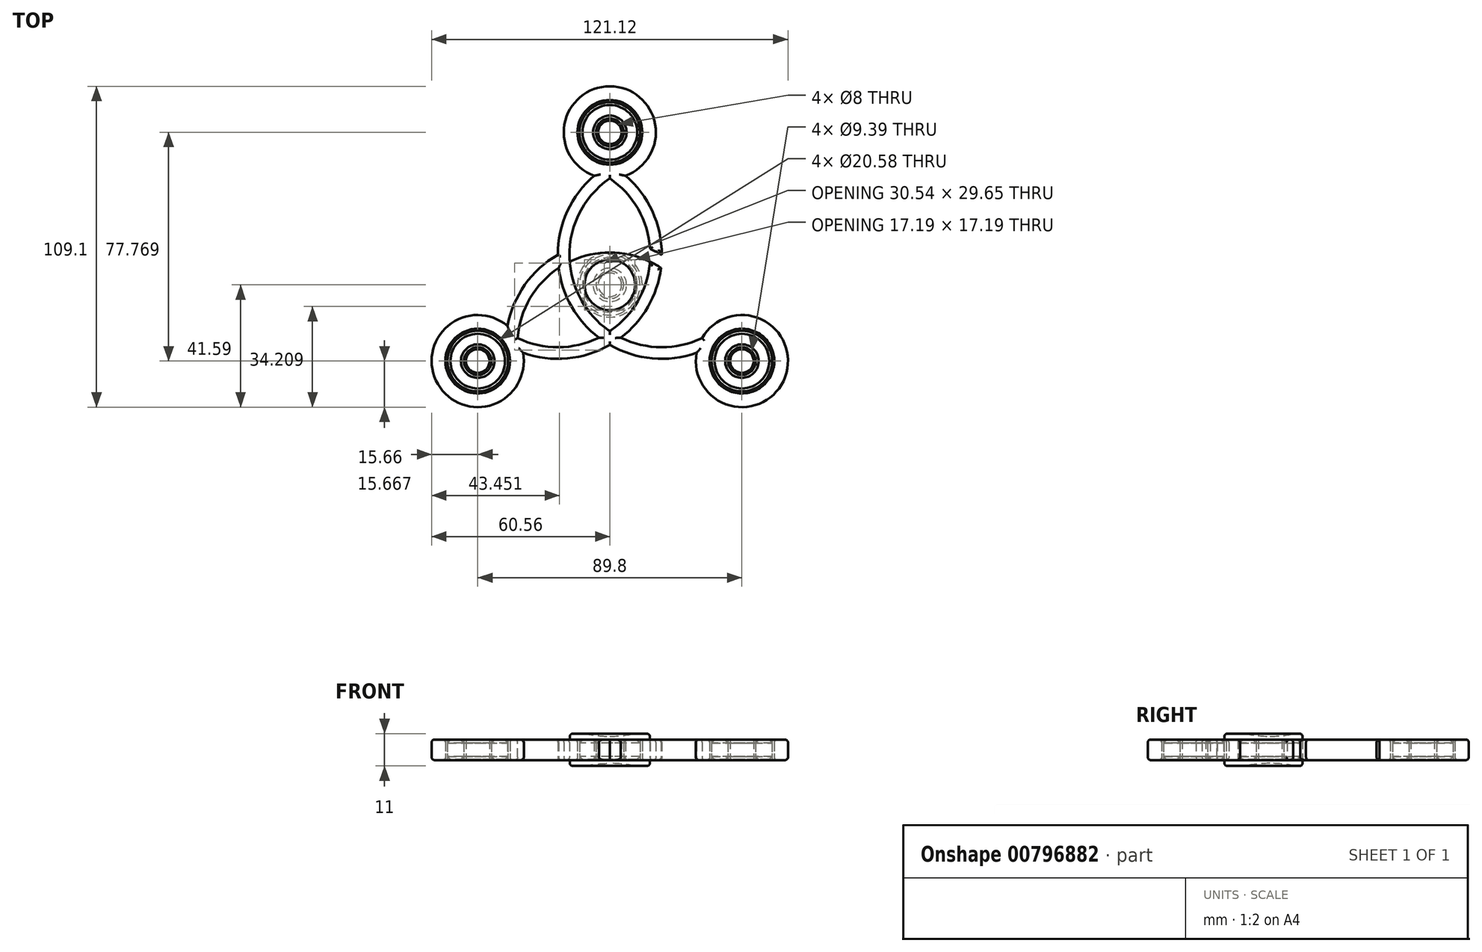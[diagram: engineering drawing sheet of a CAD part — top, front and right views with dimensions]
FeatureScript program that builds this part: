
annotation { "Feature Type Name" : "Feature", "Feature Type Description" : "" }
export const myFeature = defineFeature(function(context is Context, id is Id, definition is map)
    precondition{}
    {
        {
            var Q0;
            Q0=qCreatedBy(makeId("Front.planeOp"),FACE);
            var sketch = newSketch(context, id + "F0", { "sketchPlane" : qUnion([Q0])});
            skLineSegment(sketch, "E0", {"start": v(0, 0) * mm, "end": v(0, 16.34) * mm, "construction": true});
            skSolve(sketch);
        }
        {
            var Q0;
            Q0=qCreatedBy(makeId("Top.planeOp"),FACE);
            var sketch = newSketch(context, id + "F1", { "sketchPlane" : qUnion([Q0])});
            skCircle(sketch, "E1.cCircle", {"center": v(0, 0) * mm, "radius": 40.85 * mm, "construction": true});
            skLineSegment(sketch, "E1.0", {"start": v(0, 40.85) * mm, "end": v(35.37, -20.42) * mm, "construction": true});
            skLineSegment(sketch, "E1.1", {"start": v(35.37, -20.42) * mm, "end": v(-35.37, -20.42) * mm, "construction": true});
            skLineSegment(sketch, "E1.2", {"start": v(-35.37, -20.42) * mm, "end": v(0, 40.85) * mm, "construction": true});
            skCircle(sketch, "E2", {"center": v(0, 40.85) * mm, "radius": 11 * mm, "construction": true});
            skCircle(sketch, "E3", {"center": v(35.37, -20.42) * mm, "radius": 11 * mm, "construction": true});
            skCircle(sketch, "E4", {"center": v(-35.37, -20.42) * mm, "radius": 11 * mm, "construction": true});
            skCircle(sketch, "E5", {"center": v(0, 0) * mm, "radius": 11 * mm, "construction": true});
            skArc(sketch, "E6", {"start": v(10.27, 44.8) * mm, "mid": v(-15.33, -2.5) * mm, "end": v(35.37, -20.42) * mm});
            skArc(sketch, "E7", {"start": v(-35.37, -20.42) * mm, "mid": v(15.33, -2.5) * mm, "end": v(-10.27, 44.8) * mm});
            skArc(sketch, "E8", {"start": v(35.37, -20.42) * mm, "mid": v(0, 14.95) * mm, "end": v(-35.37, -20.42) * mm});
            skLineSegment(sketch, "E9", {"start": v(-35.37, -20.42) * mm, "end": v(-12.95, -7.48) * mm, "construction": true});
            skLineSegment(sketch, "E10.trimOffspring", {"start": v(-9.53, -5.5) * mm, "end": v(0, 0) * mm, "construction": true});
            skLineSegment(sketch, "E11", {"start": v(-12.95, -7.48) * mm, "end": v(-9.53, -5.5) * mm, "construction": true});
            skArc(sketch, "E12.0", {"start": v(11.1, 40.94) * mm, "mid": v(-11.27, -2) * mm, "end": v(35.1, -15.95) * mm});
            skArc(sketch, "E13.0", {"start": v(30.75, -26.88) * mm, "mid": v(-1.6, 10.96) * mm, "end": v(-29.93, -29.98) * mm});
            skArc(sketch, "E14.0", {"start": v(-41, -10.86) * mm, "mid": v(-40.97, -10.9) * mm, "end": v(-40.93, -10.93) * mm});
            skArc(sketch, "E15.trimOffspring", {"start": v(40.93, -10.93) * mm, "mid": v(40.97, -10.9) * mm, "end": v(41, -10.86) * mm});
            skArc(sketch, "E16.trimOffspring", {"start": v(-35.1, -15.95) * mm, "mid": v(11.27, -2) * mm, "end": v(-11.1, 40.94) * mm});
            skLineSegment(sketch, "E17", {"start": v(0, 40.85) * mm, "end": v(0, 36.18) * mm, "construction": true});
            skSolve(sketch);
        }
        {
            var Q0;
            {var subQ0=sQuery(id+"F1.wireOp",EDGE,"E13.0");var subQ1=sQuery(id+"F1.wireOp",EDGE,"E6");var subQ2=makeQuery(id+"F1.imprint","INTERSECT",VERTEX,{"disambiguationData":[OD(0.0)],"derivedFrom":[subQ1,subQ0]});Q0=makeQuery(id+"F1.imprint","IMPRINT",FACE,{"disambiguationData":[TD([[makeQuery(id+"F1.imprint","IMPRINT",EDGE,{"disambiguationData":[TD([[subQ2,1.0]])],"derivedFrom":subQ1}),1.0]])]});}
            var Q1;
            {var subQ0=sQuery(id+"F1.wireOp",EDGE,"E7");var subQ1=sQuery(id+"F1.wireOp",EDGE,"E6");var subQ2=makeQuery(id+"F1.imprint","INTERSECT",VERTEX,{"disambiguationData":[OD(1.0)],"derivedFrom":[subQ1,subQ0]});Q1=makeQuery(id+"F1.imprint","IMPRINT",FACE,{"disambiguationData":[TD([[makeQuery(id+"F1.imprint","IMPRINT",EDGE,{"disambiguationData":[TD([[subQ2,1.0]])],"derivedFrom":subQ1}),1.0]])]});}
            var Q2;
            {var subQ0=sQuery(id+"F1.wireOp",EDGE,"E7");var subQ1=sQuery(id+"F1.wireOp",EDGE,"E6");var subQ2=makeQuery(id+"F1.imprint","INTERSECT",VERTEX,{"disambiguationData":[OD(1.0)],"derivedFrom":[subQ1,subQ0]});Q2=makeQuery(id+"F1.imprint","IMPRINT",FACE,{"disambiguationData":[TD([[makeQuery(id+"F1.imprint","IMPRINT",EDGE,{"disambiguationData":[TD([[subQ2,1.0]])],"derivedFrom":subQ1}),-1.0]])]});}
            var Q3;
            {var subQ0=sQuery(id+"F1.wireOp",EDGE,"E8");var subQ1=sQuery(id+"F1.wireOp",EDGE,"E7");var subQ2=makeQuery(id+"F1.imprint","INTERSECT",VERTEX,{"disambiguationData":[OD(0.0)],"derivedFrom":[subQ1,subQ0]});Q3=makeQuery(id+"F1.imprint","IMPRINT",FACE,{"disambiguationData":[TD([[makeQuery(id+"F1.imprint","IMPRINT",EDGE,{"disambiguationData":[TD([[subQ2,-1.0]])],"derivedFrom":subQ1}),1.0]])]});}
            var Q4;
            {var subQ0=sQuery(id+"F1.wireOp",EDGE,"E8");var subQ1=sQuery(id+"F1.wireOp",EDGE,"E6");var subQ2=makeQuery(id+"F1.imprint","INTERSECT",VERTEX,{"disambiguationData":[OD(1.0)],"derivedFrom":[subQ1,subQ0]});Q4=makeQuery(id+"F1.imprint","IMPRINT",FACE,{"disambiguationData":[TD([[makeQuery(id+"F1.imprint","IMPRINT",EDGE,{"disambiguationData":[TD([[subQ2,-1.0]])],"derivedFrom":subQ1}),-1.0]])]});}
            var Q5;
            {var subQ0=sQuery(id+"F1.wireOp",EDGE,"E13.0");var subQ1=sQuery(id+"F1.wireOp",EDGE,"E6");var subQ2=makeQuery(id+"F1.imprint","INTERSECT",VERTEX,{"disambiguationData":[OD(1.0)],"derivedFrom":[subQ1,subQ0]});Q5=makeQuery(id+"F1.imprint","IMPRINT",FACE,{"disambiguationData":[TD([[makeQuery(id+"F1.imprint","IMPRINT",EDGE,{"disambiguationData":[TD([[subQ2,-1.0]])],"derivedFrom":subQ1}),1.0]])]});}
            var Q6;
            {var subQ0=sQuery(id+"F1.wireOp",EDGE,"E8");var subQ1=sQuery(id+"F1.wireOp",EDGE,"E6");var subQ2=makeQuery(id+"F1.imprint","INTERSECT",VERTEX,{"disambiguationData":[OD(1.0)],"derivedFrom":[subQ1,subQ0]});Q6=makeQuery(id+"F1.imprint","IMPRINT",FACE,{"disambiguationData":[TD([[makeQuery(id+"F1.imprint","IMPRINT",EDGE,{"disambiguationData":[TD([[subQ2,-1.0]])],"derivedFrom":subQ1}),1.0]])]});}
            var Q7;
            {var subQ0=sQuery(id+"F1.wireOp",EDGE,"E12.0");var subQ1=sQuery(id+"F1.wireOp",EDGE,"E7");var subQ2=makeQuery(id+"F1.imprint","INTERSECT",VERTEX,{"disambiguationData":[OD(1.0)],"derivedFrom":[subQ1,subQ0]});Q7=makeQuery(id+"F1.imprint","IMPRINT",FACE,{"disambiguationData":[TD([[makeQuery(id+"F1.imprint","IMPRINT",EDGE,{"disambiguationData":[TD([[subQ2,-1.0]])],"derivedFrom":subQ1}),1.0]])]});}
            var Q8;
            {var subQ0=sQuery(id+"F1.wireOp",EDGE,"E8");var subQ1=sQuery(id+"F1.wireOp",EDGE,"E6");var subQ2=makeQuery(id+"F1.imprint","INTERSECT",VERTEX,{"disambiguationData":[OD(0.0)],"derivedFrom":[subQ1,subQ0]});Q8=makeQuery(id+"F1.imprint","IMPRINT",FACE,{"disambiguationData":[TD([[makeQuery(id+"F1.imprint","IMPRINT",EDGE,{"disambiguationData":[TD([[subQ2,1.0]])],"derivedFrom":subQ1}),1.0]])]});}
            var Q9;
            {var subQ0=sQuery(id+"F1.wireOp",EDGE,"E8");var subQ1=sQuery(id+"F1.wireOp",EDGE,"E7");var subQ2=makeQuery(id+"F1.imprint","INTERSECT",VERTEX,{"disambiguationData":[OD(1.0)],"derivedFrom":[subQ1,subQ0]});Q9=makeQuery(id+"F1.imprint","IMPRINT",FACE,{"disambiguationData":[TD([[makeQuery(id+"F1.imprint","IMPRINT",EDGE,{"disambiguationData":[TD([[subQ2,1.0]])],"derivedFrom":subQ1}),-1.0]])]});}
            var Q10;
            {var subQ0=sQuery(id+"F1.wireOp",EDGE,"E8");var subQ1=sQuery(id+"F1.wireOp",EDGE,"E7");var subQ2=makeQuery(id+"F1.imprint","INTERSECT",VERTEX,{"disambiguationData":[OD(1.0)],"derivedFrom":[subQ1,subQ0]});Q10=makeQuery(id+"F1.imprint","IMPRINT",FACE,{"disambiguationData":[TD([[makeQuery(id+"F1.imprint","IMPRINT",EDGE,{"disambiguationData":[TD([[subQ2,1.0]])],"derivedFrom":subQ1}),1.0]])]});}
            var Q11;
            {var subQ0=sQuery(id+"F1.wireOp",EDGE,"E16.trimOffspring");var subQ1=sQuery(id+"F1.wireOp",EDGE,"E8");var subQ2=makeQuery(id+"F1.imprint","INTERSECT",VERTEX,{"disambiguationData":[OD(1.0)],"derivedFrom":[subQ1,subQ0]});Q11=makeQuery(id+"F1.imprint","IMPRINT",FACE,{"disambiguationData":[TD([[makeQuery(id+"F1.imprint","IMPRINT",EDGE,{"disambiguationData":[TD([[subQ2,-1.0]])],"derivedFrom":subQ1}),1.0]])]});}
            var Q12;
            {var subQ0=sQuery(id+"F1.wireOp",EDGE,"E16.trimOffspring");var subQ1=sQuery(id+"F1.wireOp",EDGE,"E6");var subQ2=makeQuery(id+"F1.imprint","INTERSECT",VERTEX,{"disambiguationData":[OD(0.0)],"derivedFrom":[subQ1,subQ0]});Q12=makeQuery(id+"F1.imprint","IMPRINT",FACE,{"disambiguationData":[TD([[makeQuery(id+"F1.imprint","IMPRINT",EDGE,{"disambiguationData":[TD([[subQ2,-1.0]])],"derivedFrom":subQ1}),1.0]])]});}
            var Q13;
            {var subQ0=sQuery(id+"F1.wireOp",EDGE,"E7");var subQ1=sQuery(id+"F1.wireOp",EDGE,"E6");var subQ2=makeQuery(id+"F1.imprint","INTERSECT",VERTEX,{"disambiguationData":[OD(0.0)],"derivedFrom":[subQ1,subQ0]});Q13=makeQuery(id+"F1.imprint","IMPRINT",FACE,{"disambiguationData":[TD([[makeQuery(id+"F1.imprint","IMPRINT",EDGE,{"disambiguationData":[TD([[subQ2,-1.0]])],"derivedFrom":subQ1}),1.0]])]});}
            var Q14;
            {var subQ0=sQuery(id+"F1.wireOp",EDGE,"E12.0");var subQ1=sQuery(id+"F1.wireOp",EDGE,"E7");var subQ2=makeQuery(id+"F1.imprint","INTERSECT",VERTEX,{"disambiguationData":[OD(0.0)],"derivedFrom":[subQ1,subQ0]});Q14=makeQuery(id+"F1.imprint","IMPRINT",FACE,{"disambiguationData":[TD([[makeQuery(id+"F1.imprint","IMPRINT",EDGE,{"disambiguationData":[TD([[subQ2,1.0]])],"derivedFrom":subQ1}),1.0]])]});}
            extrude(context, id + "F2", {"entities" : qUnion([Q0, Q1, Q2, Q3, Q4, Q5, Q6, Q7, Q8, Q9, Q10, Q11, Q12, Q13, Q14]), "endBound" : BoundingType.SYMMETRIC, "depth" : 7 * mm, "offsetDistance" : 25 * mm});
        }
        {
            var Q0;
            Q0=qCreatedBy(makeId("Top.planeOp"),FACE);
            var sketch = newSketch(context, id + "F3", { "sketchPlane" : qUnion([Q0])});
            skLineSegment(sketch, "E18", {"start": v(0, 0) * mm, "end": v(0, 40.85) * mm, "construction": true});
            skLineSegment(sketch, "E19", {"start": v(0, 40.85) * mm, "end": v(0, 51.85) * mm, "construction": true});
            skCircle(sketch, "E20", {"center": v(0, 51.85) * mm, "radius": 11 * mm});
            skCircle(sketch, "E21.0", {"center": v(0, 51.85) * mm, "radius": 15.66 * mm});
            skCircle(sketch, "E22.1.0", {"center": v(-44.9, -25.92) * mm, "radius": 11 * mm});
            skCircle(sketch, "E22.1.1", {"center": v(-44.9, -25.92) * mm, "radius": 15.66 * mm});
            skCircle(sketch, "E22.2.0", {"center": v(44.9, -25.92) * mm, "radius": 11 * mm});
            skCircle(sketch, "E22.2.1", {"center": v(44.9, -25.92) * mm, "radius": 15.66 * mm});
            skPoint(sketch, "E22.center", {"position": v(0, 0) * mm});
            skSolve(sketch);
        }
        {
            var Q0;
            Q0=qSketchRegion(id+"F3",true);
            extrude(context, id + "F4", {"entities" : qUnion([Q0]), "operationType" : NewBodyOperationType.ADD, "endBound" : BoundingType.SYMMETRIC, "depth" : 7 * mm, "offsetDistance" : 25 * mm});
        }
        {
            var Q0;
            Q0=makeQuery(id+"F4.boolean.opBoolean","MERGE",FACE,{"derivedFrom":[makeQuery(id+"F2.opExtrude","CAP_FACE",FACE,{"disambiguationData":[OSD([sQuery(id+"F1.wireOp",EDGE,"E6"),sQuery(id+"F1.wireOp",EDGE,"E7"),sQuery(id+"F1.wireOp",EDGE,"E8"),sQuery(id+"F1.wireOp",EDGE,"E12.0"),sQuery(id+"F1.wireOp",EDGE,"E13.0"),sQuery(id+"F1.wireOp",EDGE,"E16.trimOffspring")])],"isStart":true}),makeQuery(id+"F4.opExtrude","CAP_FACE",FACE,{"disambiguationData":[OSD([sQuery(id+"F3.wireOp",EDGE,"E20"),sQuery(id+"F3.wireOp",EDGE,"E21.0")])],"isStart":true}),makeQuery(id+"F4.opExtrude","CAP_FACE",FACE,{"disambiguationData":[OSD([sQuery(id+"F3.wireOp",EDGE,"E22.1.0"),sQuery(id+"F3.wireOp",EDGE,"E22.1.1")])],"isStart":true}),makeQuery(id+"F4.opExtrude","CAP_FACE",FACE,{"disambiguationData":[OSD([sQuery(id+"F3.wireOp",EDGE,"E22.2.0"),sQuery(id+"F3.wireOp",EDGE,"E22.2.1")])],"isStart":true})]});
            var Q1;
            Q1=makeQuery(id+"F4.boolean.opBoolean","MERGE",FACE,{"derivedFrom":[makeQuery(id+"F2.opExtrude","CAP_FACE",FACE,{"disambiguationData":[OSD([sQuery(id+"F1.wireOp",EDGE,"E6"),sQuery(id+"F1.wireOp",EDGE,"E7"),sQuery(id+"F1.wireOp",EDGE,"E8"),sQuery(id+"F1.wireOp",EDGE,"E12.0"),sQuery(id+"F1.wireOp",EDGE,"E13.0"),sQuery(id+"F1.wireOp",EDGE,"E16.trimOffspring")])],"isStart":false}),makeQuery(id+"F4.opExtrude","CAP_FACE",FACE,{"disambiguationData":[OSD([sQuery(id+"F3.wireOp",EDGE,"E20"),sQuery(id+"F3.wireOp",EDGE,"E21.0")])],"isStart":false}),makeQuery(id+"F4.opExtrude","CAP_FACE",FACE,{"disambiguationData":[OSD([sQuery(id+"F3.wireOp",EDGE,"E22.1.0"),sQuery(id+"F3.wireOp",EDGE,"E22.1.1")])],"isStart":false}),makeQuery(id+"F4.opExtrude","CAP_FACE",FACE,{"disambiguationData":[OSD([sQuery(id+"F3.wireOp",EDGE,"E22.2.0"),sQuery(id+"F3.wireOp",EDGE,"E22.2.1")])],"isStart":false})]});
            fillet(context, id + "F5", {"entities" : qUnion([Q0, Q1]), "radius" : 1 * mm, "tangentPropagation" : true, "allowEdgeOverflow" : false});
        }
        {
            var Q0;
            Q0=qCreatedBy(makeId("Top.planeOp"),FACE);
            var sketch = newSketch(context, id + "F6", { "sketchPlane" : qUnion([Q0])});
            skCircle(sketch, "E23", {"center": v(0, 0) * mm, "radius": 11 * mm});
            skCircle(sketch, "E24", {"center": v(0, 0) * mm, "radius": 4 * mm});
            skCircle(sketch, "E25", {"center": v(0, 0) * mm, "radius": 4.7 * mm});
            skCircle(sketch, "E26", {"center": v(0, 0) * mm, "radius": 10.3 * mm});
            skSolve(sketch);
        }
        {
            var Q0;
            Q0=makeQuery(id+"F6.imprint","IMPRINT",FACE,{"disambiguationData":[TD([[makeQuery(id+"F6.imprint","IMPRINT",EDGE,{"derivedFrom":sQuery(id+"F6.wireOp",EDGE,"E24")}),-1.0]])]});
            var Q1;
            Q1=makeQuery(id+"F6.imprint","IMPRINT",FACE,{"disambiguationData":[TD([[makeQuery(id+"F6.imprint","IMPRINT",EDGE,{"derivedFrom":sQuery(id+"F6.wireOp",EDGE,"E23")}),1.0]])]});
            extrude(context, id + "F7", {"entities" : qUnion([Q0, Q1]), "operationType" : NewBodyOperationType.ADD, "endBound" : BoundingType.SYMMETRIC, "depth" : 7 * mm, "offsetDistance" : 25 * mm});
        }
        {
            var Q0;
            Q0=makeQuery(id+"F6.imprint","IMPRINT",FACE,{"disambiguationData":[TD([[makeQuery(id+"F6.imprint","IMPRINT",EDGE,{"derivedFrom":sQuery(id+"F6.wireOp",EDGE,"E25")}),-1.0]])]});
            extrude(context, id + "F8", {"entities" : qUnion([Q0]), "endBound" : BoundingType.SYMMETRIC, "depth" : 6.5 * mm, "offsetDistance" : 25 * mm});
        }
        {
            var Q0;
            Q0=makeQuery(id+"F8.opExtrude","CAP_EDGE",EDGE,{"disambiguationData":[OSD([sQuery(id+"F6.wireOp",EDGE,"E26")])],"isStart":false});
            var Q1;
            Q1=makeQuery(id+"F8.opExtrude","CAP_EDGE",EDGE,{"disambiguationData":[OSD([sQuery(id+"F6.wireOp",EDGE,"E25")])],"isStart":false});
            chamfer(context, id + "F9", {"entities" : qUnion([Q0, Q1]), "chamferType" : ChamferType.OFFSET_ANGLE, "width" : 1 * mm, "oppositeDirection" : false, "angle" : 45 * degree, "tangentPropagation" : true});
        }
        {
            var Q0;
            Q0=makeQuery(id+"F8.opExtrude","CAP_EDGE",EDGE,{"disambiguationData":[OSD([sQuery(id+"F6.wireOp",EDGE,"E25")])],"isStart":true});
            var Q1;
            Q1=makeQuery(id+"F8.opExtrude","CAP_EDGE",EDGE,{"disambiguationData":[OSD([sQuery(id+"F6.wireOp",EDGE,"E26")])],"isStart":true});
            chamfer(context, id + "F10", {"entities" : qUnion([Q0, Q1]), "width" : 1 * mm, "tangentPropagation" : true});
        }
        {
            var Q0;
            Q0=makeQuery(id+"F7.opExtrude","CAP_EDGE",EDGE,{"disambiguationData":[OSD([sQuery(id+"F6.wireOp",EDGE,"E23")])],"isStart":false});
            var Q1;
            Q1=makeQuery(id+"F7.opExtrude","CAP_EDGE",EDGE,{"disambiguationData":[OSD([sQuery(id+"F6.wireOp",EDGE,"E26")])],"isStart":false});
            fillet(context, id + "F11", {"entities" : qUnion([Q0, Q1]), "radius" : .2 * mm, "tangentPropagation" : true, "allowEdgeOverflow" : false});
        }
        {
            var Q0;
            Q0=makeQuery(id+"F7.opExtrude","CAP_EDGE",EDGE,{"disambiguationData":[OSD([sQuery(id+"F6.wireOp",EDGE,"E24")])],"isStart":false});
            var Q1;
            Q1=makeQuery(id+"F7.opExtrude","CAP_EDGE",EDGE,{"disambiguationData":[OSD([sQuery(id+"F6.wireOp",EDGE,"E25")])],"isStart":false});
            var Q2;
            Q2=makeQuery(id+"F7.opExtrude","CAP_EDGE",EDGE,{"disambiguationData":[OSD([sQuery(id+"F6.wireOp",EDGE,"E23")])],"isStart":true});
            var Q3;
            Q3=makeQuery(id+"F7.opExtrude","CAP_EDGE",EDGE,{"disambiguationData":[OSD([sQuery(id+"F6.wireOp",EDGE,"E26")])],"isStart":true});
            var Q4;
            Q4=makeQuery(id+"F7.opExtrude","CAP_EDGE",EDGE,{"disambiguationData":[OSD([sQuery(id+"F6.wireOp",EDGE,"E25")])],"isStart":true});
            var Q5;
            Q5=makeQuery(id+"F7.opExtrude","CAP_EDGE",EDGE,{"disambiguationData":[OSD([sQuery(id+"F6.wireOp",EDGE,"E24")])],"isStart":true});
            fillet(context, id + "F12", {"entities" : qUnion([Q0, Q1, Q2, Q3, Q4, Q5]), "radius" : .2 * mm, "tangentPropagation" : true, "allowEdgeOverflow" : false});
        }
        {
            var Q0;
            Q0=qCreatedBy(makeId("Top.planeOp"),FACE);
            var sketch = newSketch(context, id + "F13", { "sketchPlane" : qUnion([Q0])});
            skLineSegment(sketch, "E27", {"start": v(0, 0) * mm, "end": v(0, 32) * mm, "construction": true});
            skSolve(sketch);
        }
        {
            var Q0;
            Q0=makeQuery(id+"F7.opExtrude","SWEPT_BODY",BODY,{"disambiguationData":[OSD([sQuery(id+"F6.wireOp",EDGE,"E23"),sQuery(id+"F6.wireOp",EDGE,"E26")])]});
            var Q1;
            Q1=makeQuery(id+"F7.opExtrude","SWEPT_BODY",BODY,{"disambiguationData":[OSD([sQuery(id+"F6.wireOp",EDGE,"E24"),sQuery(id+"F6.wireOp",EDGE,"E25")])]});
            var Q2;
            Q2=makeQuery(id+"F8.opExtrude","SWEPT_BODY",BODY,{"disambiguationData":[OSD([sQuery(id+"F6.wireOp",EDGE,"E25"),sQuery(id+"F6.wireOp",EDGE,"E26")])]});
            var Q3;
            Q3=sQuery(id+"F13.wireOp",EDGE,"E27");
            var Q4;
            Q4=sQuery(id+"F13.wireOp",EDGE,"E27");
            transform(context, id + "F14", {"entities" : qUnion([Q0, Q1, Q2]), "transformType" : TransformType.TRANSLATION_DISTANCE, "transformDirection" : qUnion([Q4]), "distance" : 51.85 * mm, "makeCopy" : true});
        }
        {
            var Q0;
            Q0=makeQuery(id+"F14.opPattern","COPY",BODY,{"derivedFrom":makeQuery(id+"F8.opExtrude","SWEPT_BODY",BODY,{"disambiguationData":[OSD([sQuery(id+"F6.wireOp",EDGE,"E25"),sQuery(id+"F6.wireOp",EDGE,"E26")])]}),"instanceName":"1"});
            var Q1;
            Q1=makeQuery(id+"F14.opPattern","COPY",BODY,{"derivedFrom":makeQuery(id+"F7.opExtrude","SWEPT_BODY",BODY,{"disambiguationData":[OSD([sQuery(id+"F6.wireOp",EDGE,"E24"),sQuery(id+"F6.wireOp",EDGE,"E25")])]}),"instanceName":"1"});
            var Q2;
            Q2=makeQuery(id+"F14.opPattern","COPY",BODY,{"derivedFrom":makeQuery(id+"F7.opExtrude","SWEPT_BODY",BODY,{"disambiguationData":[OSD([sQuery(id+"F6.wireOp",EDGE,"E23"),sQuery(id+"F6.wireOp",EDGE,"E26")])]}),"instanceName":"1"});
            var Q3;
            Q3=sQuery(id+"F0.wireOp",EDGE,"E0");
            circularPattern(context, id + "F15", {"entities" : qUnion([Q0, Q1, Q2]), "axis" : qUnion([Q3]), "angle" : 360 * degree, "instanceCount" : 3, "equalSpace" : true});
        }
        {
            var Q0;
            Q0=makeQuery(id+"F7.opExtrude","CAP_FACE",FACE,{"disambiguationData":[OSD([sQuery(id+"F6.wireOp",EDGE,"E24"),sQuery(id+"F6.wireOp",EDGE,"E25")])],"isStart":false});
            var sketch = newSketch(context, id + "F16", { "sketchPlane" : qUnion([Q0])});
            skArc(sketch, "E28.0", {"start": v(13.65, 7.88) * mm, "mid": v(0, 11) * mm, "end": v(-13.65, 7.88) * mm});
            skArc(sketch, "E29.trimOffspring", {"start": v(0, -15.76) * mm, "mid": v(9.53, -5.5) * mm, "end": v(13.65, 7.88) * mm});
            skArc(sketch, "E30.trimOffspring", {"start": v(-13.65, 7.88) * mm, "mid": v(-9.53, -5.5) * mm, "end": v(0, -15.76) * mm});
            skSolve(sketch);
        }
        {
            var Q0;
            Q0=qSketchRegion(id+"F16",true);
            extrude(context, id + "F17", {"entities" : qUnion([Q0]), "depth" : 2 * mm, "offsetDistance" : 25 * mm});
        }
        {
            var Q0;
            Q0=qCreatedBy(makeId("Front.planeOp"),FACE);
            var sketch = newSketch(context, id + "F18", { "sketchPlane" : qUnion([Q0])});
            skArc(sketch, "E31", {"start": v(0, 4.6) * mm, "mid": v(41.52, 46.12) * mm, "end": v(0, 87.64) * mm});
            skLineSegment(sketch, "E32", {"start": v(0, 46.12) * mm, "end": v(0, 4.6) * mm});
            skLineSegment(sketch, "E33", {"start": v(0, 46.12) * mm, "end": v(0, 87.64) * mm});
            skSolve(sketch);
        }
        {
            var Q0;
            Q0=makeQuery(id+"F18.imprint","IMPRINT",FACE,{"disambiguationData":[TD([[makeQuery(id+"F18.imprint","IMPRINT",EDGE,{"derivedFrom":sQuery(id+"F18.wireOp",EDGE,"E31")}),1.0]])]});
            var Q1;
            Q1=sQuery(id+"F18.wireOp",EDGE,"E33");
            revolve(context, id + "F19", {"surfaceOperationType" : NewSurfaceOperationType.NEW, "entities" : qUnion([Q0]), "axis" : qUnion([Q1]), "revolveType" : RevolveType.FULL});
        }
        {
            var Q0;
            Q0=makeQuery(id+"F19.opRevolve","SWEPT_BODY",BODY,{"disambiguationData":[OSD([sQuery(id+"F18.wireOp",EDGE,"E31"),sQuery(id+"F18.wireOp",EDGE,"E32"),sQuery(id+"F18.wireOp",EDGE,"E33")])]});
            var Q1;
            Q1=makeQuery(id+"F17.opExtrude","SWEPT_BODY",BODY,{"disambiguationData":[OSD([sQuery(id+"F16.wireOp",EDGE,"E28.0"),sQuery(id+"F16.wireOp",EDGE,"E29.trimOffspring"),sQuery(id+"F16.wireOp",EDGE,"E30.trimOffspring")])]});
            booleanBodies(context, id + "F20", {"operationType" : BooleanOperationType.SUBTRACTION, "tools" : qUnion([Q0]), "targets" : qUnion([Q1])});
        }
        {
            var Q0;
            Q0=makeQuery(id+"F17.opExtrude","CAP_EDGE",EDGE,{"disambiguationData":[OSD([sQuery(id+"F16.wireOp",EDGE,"E29.trimOffspring")])],"isStart":false});
            var Q1;
            {var subQ0=sQuery(id+"F1.wireOp",EDGE,"E16.trimOffspring");var subQ1=sQuery(id+"F1.wireOp",EDGE,"E12.0");var subQ2=sQuery(id+"F1.wireOp",EDGE,"E8");Q1=makeQuery(id+"F5.opFillet","BLEND_EDGE",EDGE,{"blendedFrom":[makeQuery(id+"F2.opExtrude","CAP_EDGE",EDGE,{"disambiguationData":[OSD([subQ2]),TDD([makeQuery(id+"F1.imprint","IMPRINT",EDGE,{"disambiguationData":[TD([[makeQuery(id+"F1.imprint","INTERSECT",VERTEX,{"disambiguationData":[OD(1.0)],"derivedFrom":[subQ2,subQ0]}),-1.0]])],"derivedFrom":subQ2})])],"isStart":false}),makeQuery(id+"F4.boolean.opBoolean","MERGE",FACE,{"derivedFrom":[makeQuery(id+"F2.opExtrude","CAP_FACE",FACE,{"disambiguationData":[OSD([sQuery(id+"F1.wireOp",EDGE,"E6"),sQuery(id+"F1.wireOp",EDGE,"E7"),subQ2,subQ1,sQuery(id+"F1.wireOp",EDGE,"E13.0"),subQ0])],"isStart":false}),makeQuery(id+"F4.opExtrude","CAP_FACE",FACE,{"disambiguationData":[OSD([sQuery(id+"F3.wireOp",EDGE,"E20"),sQuery(id+"F3.wireOp",EDGE,"E21.0")])],"isStart":false}),makeQuery(id+"F4.opExtrude","CAP_FACE",FACE,{"disambiguationData":[OSD([sQuery(id+"F3.wireOp",EDGE,"E22.1.0"),sQuery(id+"F3.wireOp",EDGE,"E22.1.1")])],"isStart":false}),makeQuery(id+"F4.opExtrude","CAP_FACE",FACE,{"disambiguationData":[OSD([sQuery(id+"F3.wireOp",EDGE,"E22.2.0"),sQuery(id+"F3.wireOp",EDGE,"E22.2.1")])],"isStart":false})]})],"blendedInto":[makeQuery(id+"F4.boolean.opBoolean","MERGE",FACE,{"derivedFrom":[makeQuery(id+"F2.opExtrude","CAP_FACE",FACE,{"disambiguationData":[OSD([sQuery(id+"F1.wireOp",EDGE,"E6"),sQuery(id+"F1.wireOp",EDGE,"E7"),subQ2,subQ1,sQuery(id+"F1.wireOp",EDGE,"E13.0"),subQ0])],"isStart":false}),makeQuery(id+"F4.opExtrude","CAP_FACE",FACE,{"disambiguationData":[OSD([sQuery(id+"F3.wireOp",EDGE,"E20"),sQuery(id+"F3.wireOp",EDGE,"E21.0")])],"isStart":false}),makeQuery(id+"F4.opExtrude","CAP_FACE",FACE,{"disambiguationData":[OSD([sQuery(id+"F3.wireOp",EDGE,"E22.1.0"),sQuery(id+"F3.wireOp",EDGE,"E22.1.1")])],"isStart":false}),makeQuery(id+"F4.opExtrude","CAP_FACE",FACE,{"disambiguationData":[OSD([sQuery(id+"F3.wireOp",EDGE,"E22.2.0"),sQuery(id+"F3.wireOp",EDGE,"E22.2.1")])],"isStart":false})]})]});}
            var Q2;
            Q2=makeQuery(id+"F17.opExtrude","CAP_EDGE",EDGE,{"disambiguationData":[OSD([sQuery(id+"F16.wireOp",EDGE,"E30.trimOffspring")])],"isStart":false});
            var Q3;
            Q3=makeQuery(id+"F17.opExtrude","SWEPT_EDGE",EDGE,{"disambiguationData":[OSD([sQuery(id+"F16.wireOp",EDGE,"E29.trimOffspring"),sQuery(id+"F16.wireOp",EDGE,"E30.trimOffspring")])]});
            var Q4;
            Q4=makeQuery(id+"F17.opExtrude","SWEPT_EDGE",EDGE,{"disambiguationData":[OSD([sQuery(id+"F16.wireOp",EDGE,"E28.0"),sQuery(id+"F16.wireOp",EDGE,"E29.trimOffspring")])]});
            var Q5;
            Q5=makeQuery(id+"F17.opExtrude","CAP_EDGE",EDGE,{"disambiguationData":[OSD([sQuery(id+"F16.wireOp",EDGE,"E28.0")])],"isStart":false});
            var Q6;
            Q6=makeQuery(id+"F17.opExtrude","SWEPT_EDGE",EDGE,{"disambiguationData":[OSD([sQuery(id+"F16.wireOp",EDGE,"E28.0"),sQuery(id+"F16.wireOp",EDGE,"E30.trimOffspring")])]});
            fillet(context, id + "F21", {"entities" : qUnion([Q0, Q1, Q2, Q3, Q4, Q5, Q6]), "radius" : 1 * mm, "tangentPropagation" : true, "allowEdgeOverflow" : false});
        }
        {
            var Q0;
            Q0=makeQuery(id+"F17.opExtrude","SWEPT_BODY",BODY,{"disambiguationData":[OSD([sQuery(id+"F16.wireOp",EDGE,"E28.0"),sQuery(id+"F16.wireOp",EDGE,"E29.trimOffspring"),sQuery(id+"F16.wireOp",EDGE,"E30.trimOffspring")])]});
            var Q1;
            Q1=qCreatedBy(makeId("Top.planeOp"),FACE);
            mirror(context, id + "F22", {"entities" : qUnion([Q0]), "mirrorPlane" : qUnion([Q1])});
        }
    });
